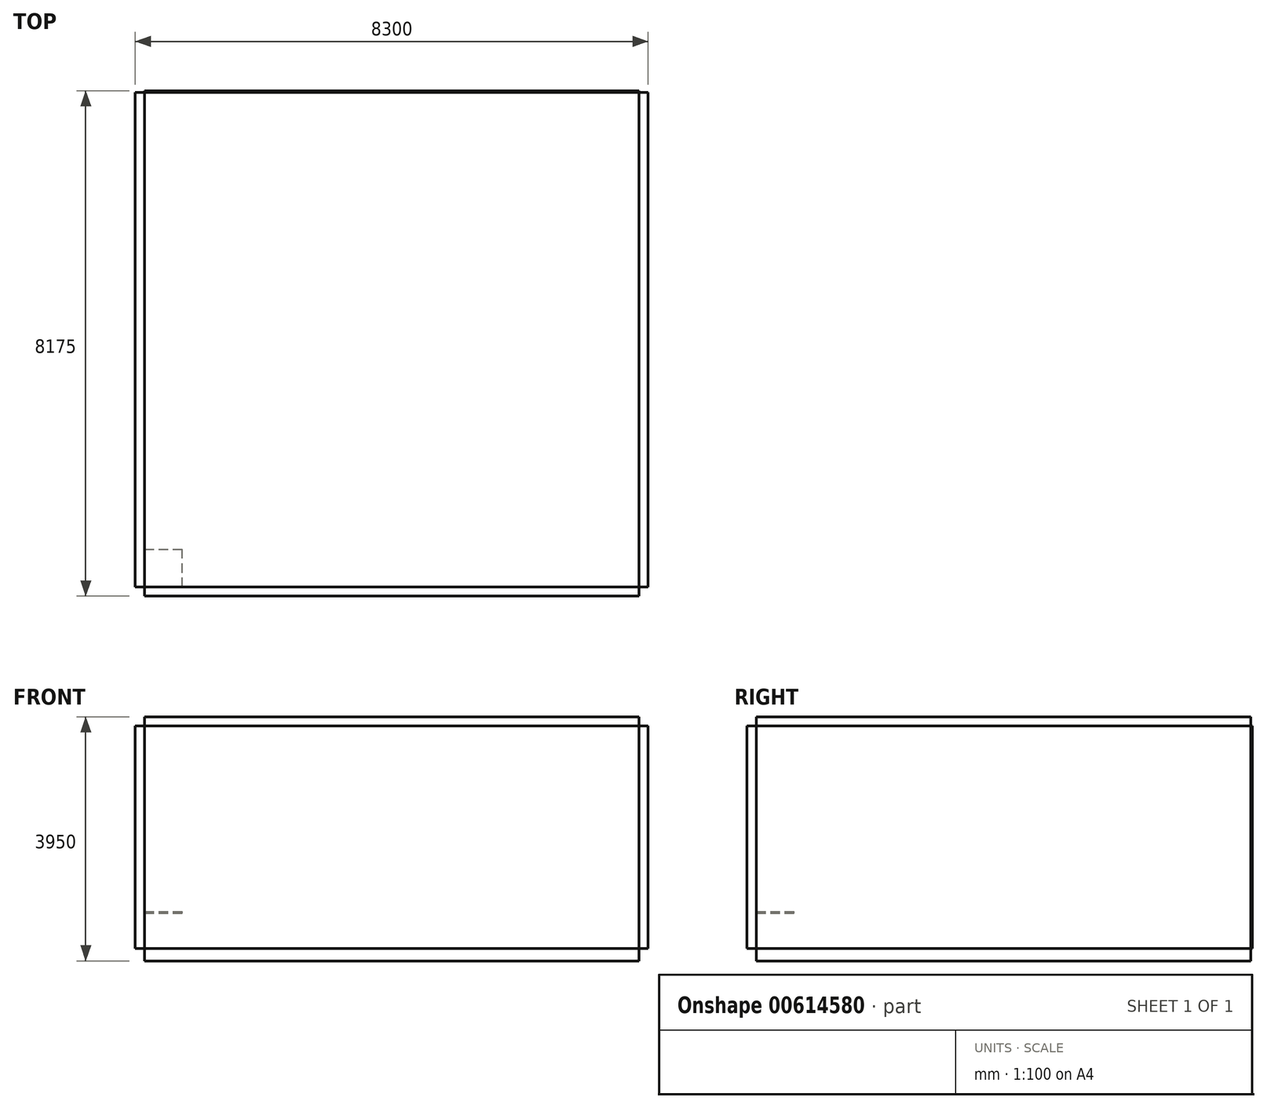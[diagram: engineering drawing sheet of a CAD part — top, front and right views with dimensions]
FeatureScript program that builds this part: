
annotation { "Feature Type Name" : "Feature", "Feature Type Description" : "" }
export const myFeature = defineFeature(function(context is Context, id is Id, definition is map)
    precondition{}
    {
        {
            var Q0;
            Q0=qCreatedBy(makeId("Top.planeOp"),FACE);
            var sketch = newSketch(context, id + "F0", { "sketchPlane" : qUnion([Q0])});
            skLineSegment(sketch, "E0.bottom", {"start": v(0, 0) * mm, "end": v(8000, 0) * mm});
            skLineSegment(sketch, "E0.top", {"start": v(0, 8000) * mm, "end": v(8000, 8000) * mm});
            skLineSegment(sketch, "E0.left", {"start": v(0, 0) * mm, "end": v(0, 8000) * mm});
            skLineSegment(sketch, "E0.right", {"start": v(8000, 0) * mm, "end": v(8000, 8000) * mm});
            skSolve(sketch);
        }
        {
            var Q0;
            Q0=qCreatedBy(makeId("Right.planeOp"),FACE);
            var sketch = newSketch(context, id + "F1", { "sketchPlane" : qUnion([Q0])});
            skLineSegment(sketch, "E1.bottom", {"start": v(0, 0) * mm, "end": v(8000, 0) * mm});
            skLineSegment(sketch, "E1.top", {"start": v(0, 3600) * mm, "end": v(8000, 3600) * mm});
            skLineSegment(sketch, "E1.left", {"start": v(0, 0) * mm, "end": v(0, 3600) * mm});
            skLineSegment(sketch, "E1.right", {"start": v(8000, 0) * mm, "end": v(8000, 3600) * mm});
            skSolve(sketch);
        }
        {
            var Q0;
            Q0=qCreatedBy(makeId("Front.planeOp"),FACE);
            var sketch = newSketch(context, id + "F2", { "sketchPlane" : qUnion([Q0])});
            skLineSegment(sketch, "E2.bottom", {"start": v(0, 0) * mm, "end": v(8000, 0) * mm});
            skLineSegment(sketch, "E2.top", {"start": v(0, 3600) * mm, "end": v(8000, 3600) * mm});
            skLineSegment(sketch, "E2.left", {"start": v(0, 0) * mm, "end": v(0, 3600) * mm});
            skLineSegment(sketch, "E2.right", {"start": v(8000, 0) * mm, "end": v(8000, 3600) * mm});
            skSolve(sketch);
        }
        {
            var Q0;
            Q0=sQuery(id+"F1.wireOp",VERTEX,"E1.right.end");
            var Q1;
            Q1=sQuery(id+"F1.wireOp",VERTEX,"E1.right.start");
            var Q2;
            Q2=sQuery(id+"F0.wireOp",VERTEX,"E0.right.end");
            cPlane(context, id + "F3", {"entities" : qUnion([Q0, Q1, Q2]), "cplaneType" : CPlaneType.THREE_POINT, "offset" : 25 * mm, "width" : 150 * mm, "height" : 150 * mm});
        }
        {
            var Q0;
            Q0=sQuery(id+"F2.wireOp",VERTEX,"E2.right.end");
            var Q1;
            Q1=sQuery(id+"F2.wireOp",VERTEX,"E2.right.start");
            var Q2;
            Q2=sQuery(id+"F0.wireOp",VERTEX,"E0.top.end");
            cPlane(context, id + "F4", {"entities" : qUnion([Q0, Q1, Q2]), "cplaneType" : CPlaneType.THREE_POINT, "offset" : 25 * mm, "width" : 150 * mm, "height" : 150 * mm});
        }
        {
            var Q0;
            Q0=sQuery(id+"F1.wireOp",VERTEX,"E1.right.end");
            var Q1;
            Q1=sQuery(id+"F2.wireOp",VERTEX,"E2.left.end");
            var Q2;
            Q2=sQuery(id+"F2.wireOp",VERTEX,"E2.right.end");
            cPlane(context, id + "F5", {"entities" : qUnion([Q0, Q1, Q2]), "cplaneType" : CPlaneType.THREE_POINT, "offset" : 25 * mm, "width" : 150 * mm, "height" : 150 * mm});
        }
        {
            var Q0;
            Q0=qCreatedBy(makeId("Top.planeOp"),FACE);
            cPlane(context, id + "F6", {"entities" : qUnion([Q0]), "cplaneType" : CPlaneType.OFFSET, "offset" : 600 * mm, "width" : 150 * mm, "height" : 150 * mm});
        }
        {
            var Q0;
            Q0=qCreatedBy(id+"F6.planeOp",FACE);
            var sketch = newSketch(context, id + "F7", { "sketchPlane" : qUnion([Q0])});
            skLineSegment(sketch, "E3.bottom", {"start": v(0, 0) * mm, "end": v(610, 0) * mm});
            skLineSegment(sketch, "E3.top", {"start": v(0, 610) * mm, "end": v(610, 610) * mm});
            skLineSegment(sketch, "E3.left", {"start": v(0, 0) * mm, "end": v(0, 610) * mm});
            skLineSegment(sketch, "E3.right", {"start": v(610, 0) * mm, "end": v(610, 610) * mm});
            skSolve(sketch);
        }
        {
            var Q0;
            Q0=makeQuery(id+"F1.imprint","IMPRINT",FACE,{"disambiguationData":[TD([[makeQuery(id+"F1.imprint","IMPRINT",EDGE,{"derivedFrom":sQuery(id+"F1.wireOp",EDGE,"E1.bottom")}),1.0]])]});
            extrude(context, id + "F8", {"entities" : qUnion([Q0]), "oppositeDirection" : true, "depth" : 150 * mm, "offsetDistance" : 25 * mm});
        }
        {
            var Q0;
            Q0=makeQuery(id+"F2.imprint","IMPRINT",FACE,{"disambiguationData":[TD([[makeQuery(id+"F2.imprint","IMPRINT",EDGE,{"derivedFrom":sQuery(id+"F2.wireOp",EDGE,"E2.bottom")}),1.0]])]});
            extrude(context, id + "F9", {"entities" : qUnion([Q0]), "depth" : 150 * mm, "offsetDistance" : 25 * mm});
        }
        {
            var Q0;
            Q0=makeQuery(id+"F0.imprint","IMPRINT",FACE,{"disambiguationData":[TD([[makeQuery(id+"F0.imprint","IMPRINT",EDGE,{"derivedFrom":sQuery(id+"F0.wireOp",EDGE,"E0.bottom")}),1.0]])]});
            extrude(context, id + "F10", {"entities" : qUnion([Q0]), "oppositeDirection" : true, "depth" : 200 * mm, "offsetDistance" : 25 * mm});
        }
        {
            var Q0;
            Q0=qCreatedBy(id+"F4.planeOp",FACE);
            var sketch = newSketch(context, id + "F11", { "sketchPlane" : qUnion([Q0])});
            skLineSegment(sketch, "E4.bottom", {"start": v(0, 0) * mm, "end": v(-8000, 0) * mm});
            skLineSegment(sketch, "E4.top", {"start": v(0, 3600) * mm, "end": v(-8000, 3600) * mm});
            skLineSegment(sketch, "E4.left", {"start": v(0, 0) * mm, "end": v(0, 3600) * mm});
            skLineSegment(sketch, "E4.right", {"start": v(-8000, 0) * mm, "end": v(-8000, 3600) * mm});
            skSolve(sketch);
        }
        {
            var Q0;
            Q0=qCreatedBy(id+"F3.planeOp",FACE);
            var sketch = newSketch(context, id + "F12", { "sketchPlane" : qUnion([Q0])});
            skLineSegment(sketch, "E5.bottom", {"start": v(0, 0) * mm, "end": v(-8000, 0) * mm});
            skLineSegment(sketch, "E5.top", {"start": v(0, 3600) * mm, "end": v(-8000, 3600) * mm});
            skLineSegment(sketch, "E5.left", {"start": v(0, 0) * mm, "end": v(0, 3600) * mm});
            skLineSegment(sketch, "E5.right", {"start": v(-8000, 0) * mm, "end": v(-8000, 3600) * mm});
            skSolve(sketch);
        }
        {
            var Q0;
            Q0=qCreatedBy(id+"F5.planeOp",FACE);
            var sketch = newSketch(context, id + "F13", { "sketchPlane" : qUnion([Q0])});
            skLineSegment(sketch, "E6.bottom", {"start": v(0, 0) * mm, "end": v(8000, 0) * mm});
            skLineSegment(sketch, "E6.top", {"start": v(0, -8000) * mm, "end": v(8000, -8000) * mm});
            skLineSegment(sketch, "E6.left", {"start": v(0, 0) * mm, "end": v(0, -8000) * mm});
            skLineSegment(sketch, "E6.right", {"start": v(8000, 0) * mm, "end": v(8000, -8000) * mm});
            skSolve(sketch);
        }
        {
            var Q0;
            Q0=makeQuery(id+"F11.imprint","IMPRINT",FACE,{"disambiguationData":[TD([[makeQuery(id+"F11.imprint","IMPRINT",EDGE,{"derivedFrom":sQuery(id+"F11.wireOp",EDGE,"E4.bottom")}),-1.0]])]});
            extrude(context, id + "F14", {"entities" : qUnion([Q0]), "oppositeDirection" : true, "depth" : 150 * mm, "offsetDistance" : 25 * mm});
        }
        {
            var Q0;
            Q0=makeQuery(id+"F12.imprint","IMPRINT",FACE,{"disambiguationData":[TD([[makeQuery(id+"F12.imprint","IMPRINT",EDGE,{"derivedFrom":sQuery(id+"F12.wireOp",EDGE,"E5.bottom")}),-1.0]])]});
            extrude(context, id + "F15", {"entities" : qUnion([Q0]), "depth" : 25 * mm, "offsetDistance" : 25 * mm});
        }
        {
            var Q0;
            Q0=makeQuery(id+"F13.imprint","IMPRINT",FACE,{"disambiguationData":[TD([[makeQuery(id+"F13.imprint","IMPRINT",EDGE,{"derivedFrom":sQuery(id+"F13.wireOp",EDGE,"E6.bottom")}),-1.0]])]});
            extrude(context, id + "F16", {"entities" : qUnion([Q0]), "oppositeDirection" : true, "depth" : 150 * mm, "offsetDistance" : 25 * mm});
        }
        {
            var Q0;
            Q0=makeQuery(id+"F7.imprint","IMPRINT",FACE,{"disambiguationData":[TD([[makeQuery(id+"F7.imprint","IMPRINT",EDGE,{"derivedFrom":sQuery(id+"F7.wireOp",EDGE,"E3.bottom")}),1.0]])]});
            extrude(context, id + "F17", {"entities" : qUnion([Q0]), "oppositeDirection" : true, "depth" : 25 * mm, "offsetDistance" : 25 * mm});
        }
    });
